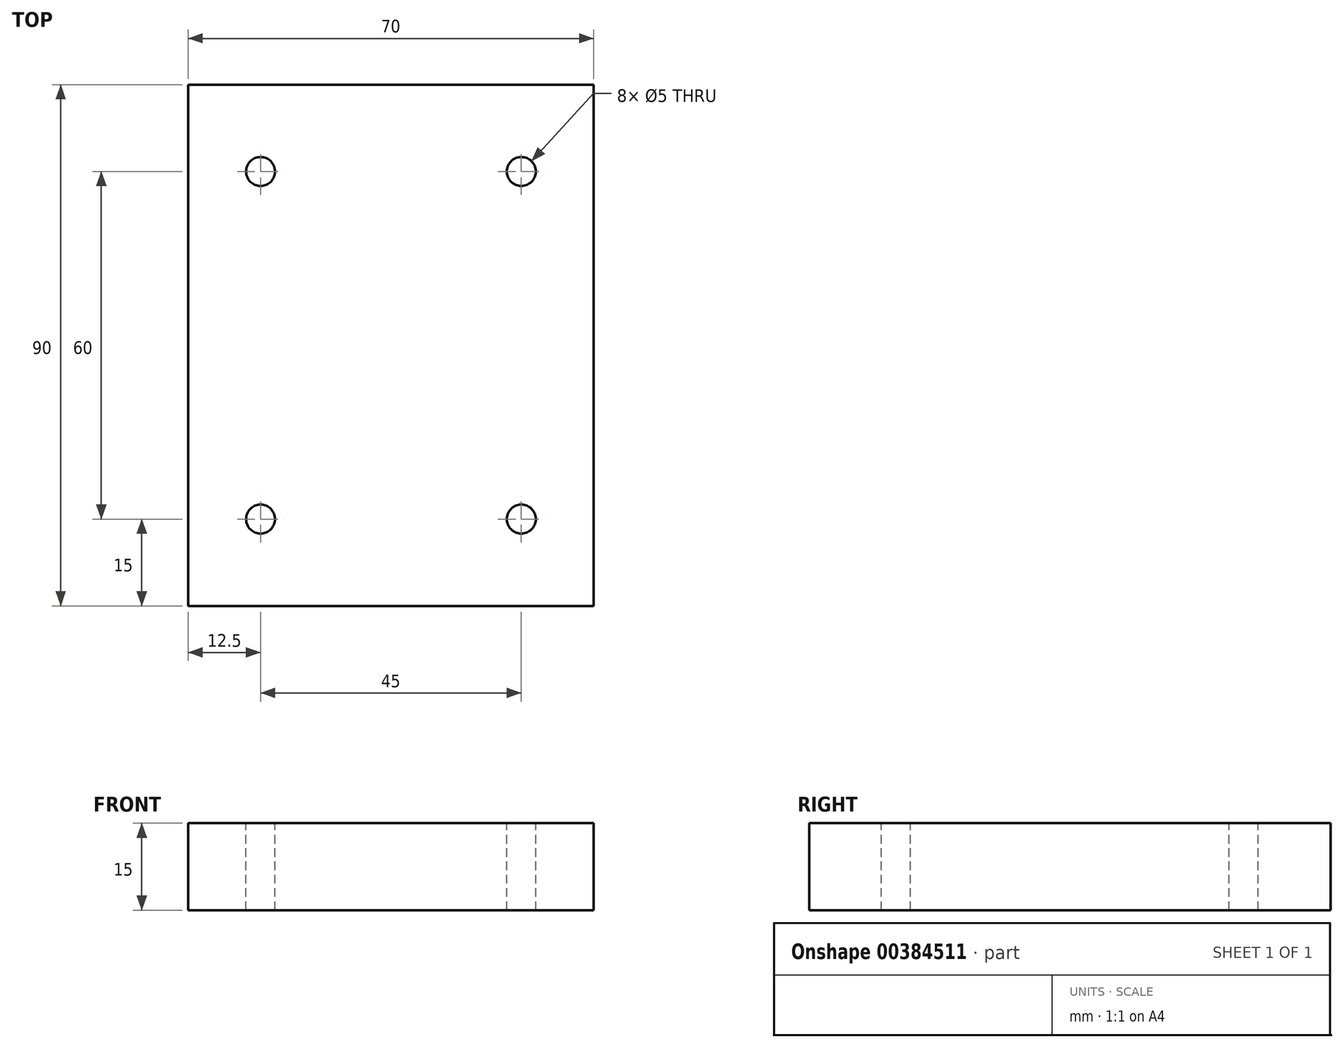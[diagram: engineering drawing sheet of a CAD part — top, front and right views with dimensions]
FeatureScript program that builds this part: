
annotation { "Feature Type Name" : "Feature", "Feature Type Description" : "" }
export const myFeature = defineFeature(function(context is Context, id is Id, definition is map)
    precondition{}
    {
        {
            var Q0;
            Q0=qCreatedBy(makeId("Top.planeOp"),FACE);
            var sketch = newSketch(context, id + "F0", { "sketchPlane" : qUnion([Q0])});
            skLineSegment(sketch, "E0.bottom", {"start": v(35, 45) * mm, "end": v(-35, 45) * mm});
            skLineSegment(sketch, "E0.top", {"start": v(35, -45) * mm, "end": v(-35, -45) * mm});
            skLineSegment(sketch, "E0.left", {"start": v(35, 45) * mm, "end": v(35, -45) * mm});
            skLineSegment(sketch, "E0.right", {"start": v(-35, 45) * mm, "end": v(-35, -45) * mm});
            skPoint(sketch, "E0.middle", {"position": v(0, 0) * mm});
            skSolve(sketch);
        }
        {
            var Q0;
            Q0=makeQuery(id+"F0.imprint","IMPRINT",FACE,{"disambiguationData":[TD([[makeQuery(id+"F0.imprint","IMPRINT",EDGE,{"derivedFrom":sQuery(id+"F0.wireOp",EDGE,"E0.bottom")}),1.0]])]});
            extrude(context, id + "F1", {"entities" : qUnion([Q0]), "depth" : 15 * mm});
        }
        {
            var Q0;
            Q0=makeQuery(id+"F1.opExtrude","CAP_FACE",FACE,{"disambiguationData":[OSD([sQuery(id+"F0.wireOp",EDGE,"E0.bottom"),sQuery(id+"F0.wireOp",EDGE,"E0.top"),sQuery(id+"F0.wireOp",EDGE,"E0.left"),sQuery(id+"F0.wireOp",EDGE,"E0.right")])],"isStart":false});
            var sketch = newSketch(context, id + "F2", { "sketchPlane" : qUnion([Q0])});
            skLineSegment(sketch, "E1", {"start": v(35, -45) * mm, "end": v(35, -30) * mm, "construction": true});
            skLineSegment(sketch, "E2", {"start": v(35, -30) * mm, "end": v(22.5, -30) * mm, "construction": true});
            skLineSegment(sketch, "E3", {"start": v(22.5, -30) * mm, "end": v(-22.5, -30) * mm, "construction": true});
            skLineSegment(sketch, "E4", {"start": v(35, 0) * mm, "end": v(-35, 0) * mm, "construction": true});
            skLineSegment(sketch, "E5.MirrorCS", {"start": v(22.5, 30) * mm, "end": v(-22.5, 30) * mm, "construction": true});
            skSolve(sketch);
        }
        {
            var Q0;
            Q0=sQuery(id+"F2.wireOp",VERTEX,"E3.end");
            var Q1;
            Q1=sQuery(id+"F2.wireOp",VERTEX,"E3.start");
            var Q2;
            Q2=sQuery(id+"F2.wireOp",VERTEX,"E5.MirrorCS.start");
            var Q3;
            Q3=sQuery(id+"F2.wireOp",VERTEX,"E5.MirrorCS.end");
            var Q4;
            Q4=makeQuery(id+"F1.opExtrude","SWEPT_BODY",BODY,{"disambiguationData":[OSD([sQuery(id+"F0.wireOp",EDGE,"E0.bottom"),sQuery(id+"F0.wireOp",EDGE,"E0.top"),sQuery(id+"F0.wireOp",EDGE,"E0.left"),sQuery(id+"F0.wireOp",EDGE,"E0.right")])]});
            hole(context, id + "F3", {"style" : HoleStyle.SIMPLE, "endStyle" : HoleEndStyle.BLIND, "holeDiameter" : 5 * mm, "holeDepth" : 25 * mm, "isTappedThrough" : true, "tappedDepth" : 12 * mm, "tapClearance" : 3, "locations" : qUnion([Q0, Q1, Q2, Q3]), "scope" : qUnion([Q4])});
        }
    });
